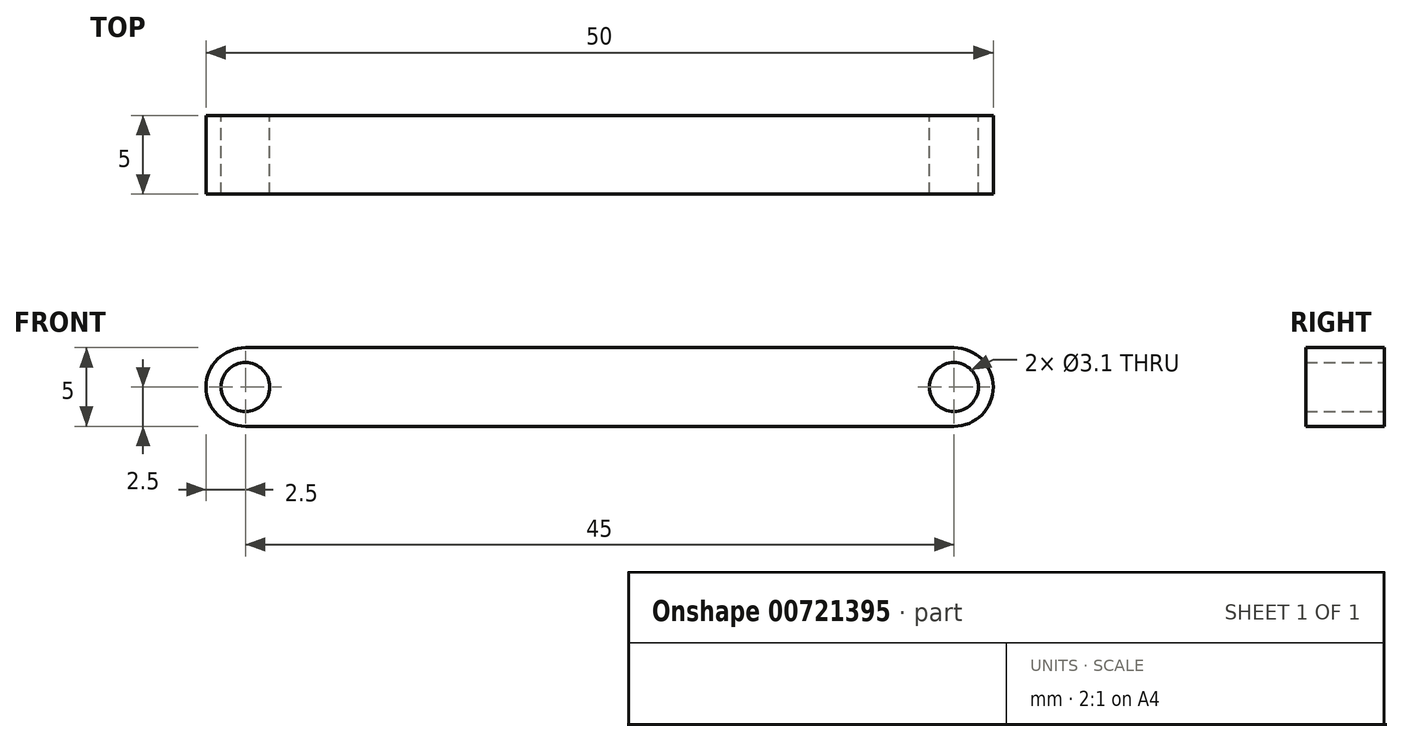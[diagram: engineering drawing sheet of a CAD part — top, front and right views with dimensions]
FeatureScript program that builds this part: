
annotation { "Feature Type Name" : "Feature", "Feature Type Description" : "" }
export const myFeature = defineFeature(function(context is Context, id is Id, definition is map)
    precondition{}
    {
        {
            var Q0;
            Q0=qCreatedBy(makeId("Front.planeOp"),FACE);
            var sketch = newSketch(context, id + "F0", { "sketchPlane" : qUnion([Q0])});
            skLineSegment(sketch, "E0.bottom", {"start": v(-25, 2.5) * mm, "end": v(25, 2.5) * mm});
            skLineSegment(sketch, "E0.top", {"start": v(-25, -2.5) * mm, "end": v(25, -2.5) * mm});
            skLineSegment(sketch, "E0.left", {"start": v(-25, 2.5) * mm, "end": v(-25, -2.5) * mm});
            skLineSegment(sketch, "E0.right", {"start": v(25, 2.5) * mm, "end": v(25, -2.5) * mm});
            skPoint(sketch, "E0.middle", {"position": v(0, 0) * mm});
            skSolve(sketch);
        }
        {
            var Q0;
            Q0 = qSketchRegion(id + "F0", true);
            extrude(context, id + "F1", {"entities" : qUnion([Q0]), "endBound" : BoundingType.SYMMETRIC, "depth" : 5 * mm, "offsetDistance" : 25 * mm});
        }
        {
            var Q0;
            Q0=makeQuery(id+"F1.opExtrude","SWEPT_EDGE",EDGE,{"disambiguationData":[OSD([sQuery(id+"F0.wireOp",EDGE,"E0.bottom"),sQuery(id+"F0.wireOp",EDGE,"E0.right")])]});
            var Q1;
            Q1=makeQuery(id+"F1.opExtrude","SWEPT_EDGE",EDGE,{"disambiguationData":[OSD([sQuery(id+"F0.wireOp",EDGE,"E0.top"),sQuery(id+"F0.wireOp",EDGE,"E0.right")])]});
            var Q2;
            Q2=makeQuery(id+"F1.opExtrude","SWEPT_EDGE",EDGE,{"disambiguationData":[OSD([sQuery(id+"F0.wireOp",EDGE,"E0.bottom"),sQuery(id+"F0.wireOp",EDGE,"E0.left")])]});
            var Q3;
            Q3=makeQuery(id+"F1.opExtrude","SWEPT_EDGE",EDGE,{"disambiguationData":[OSD([sQuery(id+"F0.wireOp",EDGE,"E0.top"),sQuery(id+"F0.wireOp",EDGE,"E0.left")])]});
            fillet(context, id + "F2", {"entities" : qUnion([Q0, Q1, Q2, Q3]), "radius" : 2.5 * mm, "tangentPropagation" : true, "allowEdgeOverflow" : false});
        }
        {
            var Q0;
            Q0=makeQuery(id+"F1.opExtrude","CAP_FACE",FACE,{"disambiguationData":[OSD([sQuery(id+"F0.wireOp",EDGE,"E0.bottom"),sQuery(id+"F0.wireOp",EDGE,"E0.top"),sQuery(id+"F0.wireOp",EDGE,"E0.left"),sQuery(id+"F0.wireOp",EDGE,"E0.right")])],"isStart":true});
            var sketch = newSketch(context, id + "F3", { "sketchPlane" : qUnion([Q0])});
            skCircle(sketch, "E1", {"center": v(-22.5, 0) * mm, "radius": 1.55 * mm});
            skCircle(sketch, "E2", {"center": v(22.5, 0) * mm, "radius": 1.55 * mm});
            skSolve(sketch);
        }
        {
            var Q0;
            Q0=makeQuery(id+"F3.imprint","IMPRINT",FACE,{"disambiguationData":[TD([[makeQuery(id+"F3.imprint","IMPRINT",EDGE,{"derivedFrom":sQuery(id+"F3.wireOp",EDGE,"E1")}),1.0]])]});
            var Q1;
            Q1=makeQuery(id+"F3.imprint","IMPRINT",FACE,{"disambiguationData":[TD([[makeQuery(id+"F3.imprint","IMPRINT",EDGE,{"derivedFrom":sQuery(id+"F3.wireOp",EDGE,"E2")}),1.0]])]});
            var Q2;
            Q2=sQuery(id+"F3.wireOp",EDGE,"E2");
            var Q3;
            Q3=sQuery(id+"F3.wireOp",EDGE,"E1");
            extrude(context, id + "F4", {"entities" : qUnion([Q0, Q1]), "operationType" : NewBodyOperationType.REMOVE, "surfaceEntities" : qUnion([Q2, Q3]), "endBound" : BoundingType.SYMMETRIC, "oppositeDirection" : true, "depth" : 25 * mm, "offsetDistance" : 25 * mm});
        }
    });
